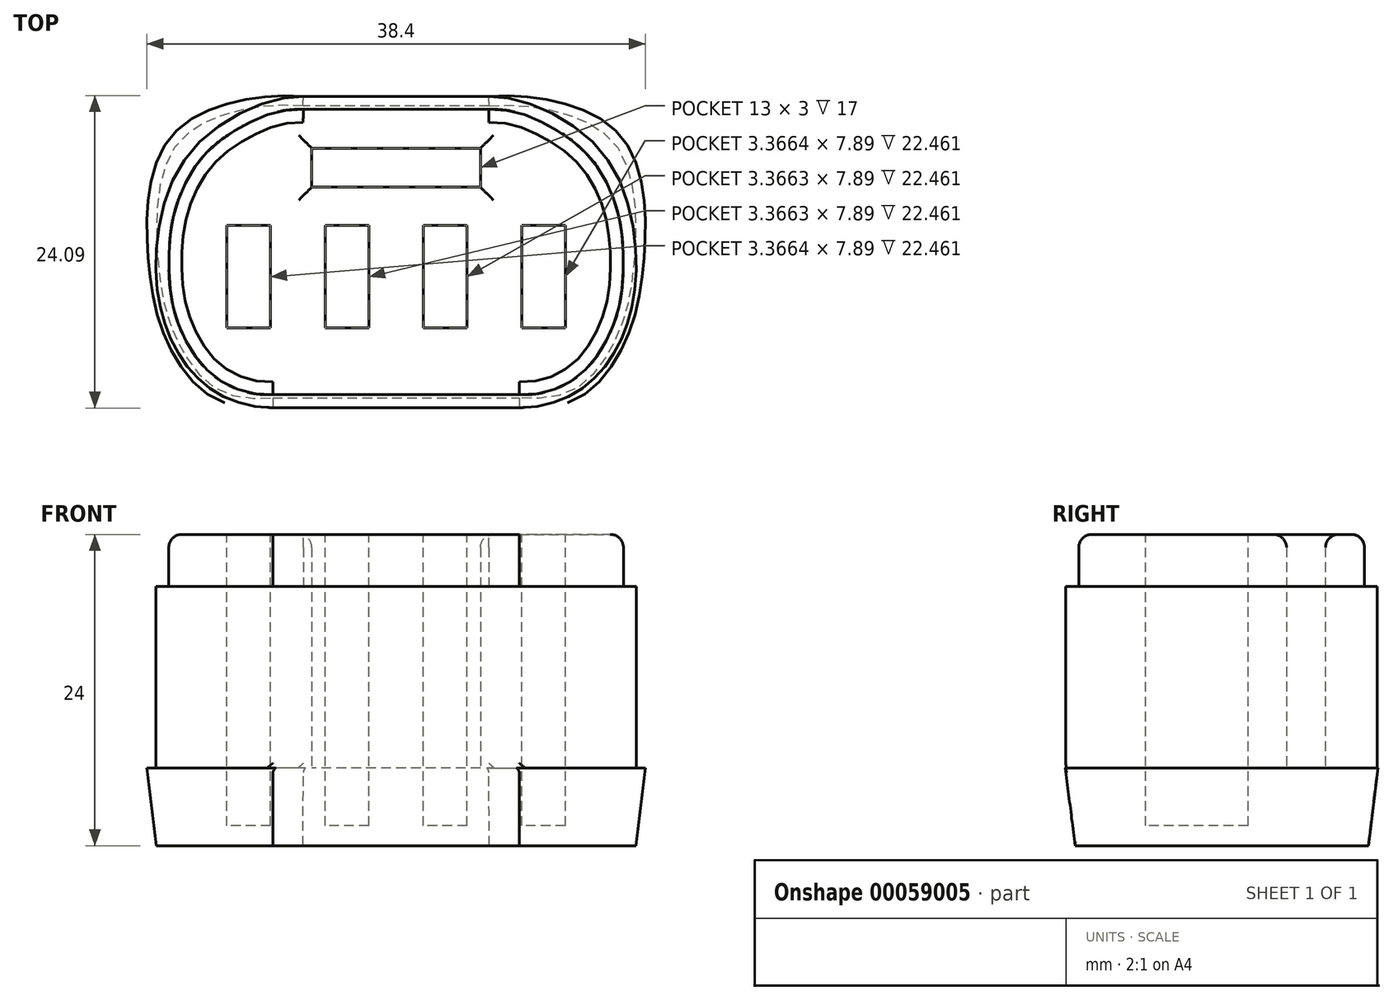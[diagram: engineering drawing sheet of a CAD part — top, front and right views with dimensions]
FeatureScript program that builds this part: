
annotation { "Feature Type Name" : "Feature", "Feature Type Description" : "" }
export const myFeature = defineFeature(function(context is Context, id is Id, definition is map)
    precondition{}
    {
        {
            var Q0;
            Q0=qCreatedBy(makeId("Top.planeOp"),FACE);
            var sketch = newSketch(context, id + "F0", { "sketchPlane" : qUnion([Q0])});
            skLineSegment(sketch, "E0", {"start": v(-18.5, 34.36) * mm, "end": v(18.5, 34.36) * mm, "construction": true});
            skLineSegment(sketch, "E1", {"start": v(0, 34.36) * mm, "end": v(0, 0) * mm, "construction": true});
            skLineSegment(sketch, "E2", {"start": v(0, 47.7) * mm, "end": v(0, 23.7) * mm, "construction": true});
            skLineSegment(sketch, "E3", {"start": v(0, 47.7) * mm, "end": v(7.15, 47.7) * mm});
            skLineSegment(sketch, "E4", {"start": v(0, 47.7) * mm, "end": v(-7.15, 47.7) * mm});
            skLineSegment(sketch, "E5", {"start": v(0, 23.7) * mm, "end": v(9.49, 23.7) * mm});
            skLineSegment(sketch, "E6", {"start": v(0, 23.7) * mm, "end": v(-9.49, 23.7) * mm});
            skFitSpline(sketch, "E7", {"points": [v(7.15, 47.7) * mm, v(15.73, 43.56) * mm, v(18.5, 34.36) * mm, v(17.25, 28.75) * mm, v(14.33, 25.17) * mm, v(9.49, 23.7) * mm], "startDerivative": vector(32.68, 0) * mm, "endDerivative": vector(-32.43, 0) * mm});
            skFitSpline(sketch, "E8.MirrorCS", {"points": [v(-7.15, 47.7) * mm, v(-15.73, 43.56) * mm, v(-18.5, 34.36) * mm, v(-17.25, 28.75) * mm, v(-14.33, 25.17) * mm, v(-9.49, 23.7) * mm], "startDerivative": vector(-32.68, 0) * mm, "endDerivative": vector(32.43, 0) * mm});
            skLineSegment(sketch, "E9.0", {"start": v(0, 46.7) * mm, "end": v(-7.15, 46.7) * mm});
            skFitSpline(sketch, "E10.0", {"points": [v(-7.15, 46.7) * mm, v(-7.73, 46.7) * mm, v(-9.1, 46.5) * mm, v(-11.02, 45.8) * mm, v(-12.5, 45) * mm, v(-13.55, 44.28) * mm, v(-14.5, 43.46) * mm, v(-15.28, 42.56) * mm, v(-15.93, 41.55) * mm, v(-16.64, 40.1) * mm, v(-17.22, 38.14) * mm, v(-17.47, 36.14) * mm, v(-17.51, 34.63) * mm, v(-17.48, 33.57) * mm, v(-17.38, 32.6) * mm, v(-17.22, 31.7) * mm, v(-17, 30.85) * mm, v(-16.74, 30.05) * mm, v(-16.41, 29.3) * mm, v(-15.9, 28.33) * mm, v(-15.16, 27.23) * mm, v(-14.06, 26.14) * mm, v(-12.76, 25.33) * mm, v(-11.24, 24.82) * mm, v(-10.1, 24.7) * mm, v(-9.49, 24.7) * mm]});
            skLineSegment(sketch, "E10.1", {"start": v(0, 46.7) * mm, "end": v(7.15, 46.7) * mm});
            skFitSpline(sketch, "E10.2", {"points": [v(7.15, 46.7) * mm, v(7.73, 46.7) * mm, v(9.1, 46.5) * mm, v(11.02, 45.8) * mm, v(12.5, 45) * mm, v(13.55, 44.28) * mm, v(14.5, 43.46) * mm, v(15.28, 42.56) * mm, v(15.93, 41.55) * mm, v(16.64, 40.1) * mm, v(17.22, 38.14) * mm, v(17.47, 36.14) * mm, v(17.51, 34.63) * mm, v(17.48, 33.57) * mm, v(17.38, 32.6) * mm, v(17.22, 31.7) * mm, v(17, 30.85) * mm, v(16.74, 30.05) * mm, v(16.41, 29.3) * mm, v(15.9, 28.33) * mm, v(15.16, 27.23) * mm, v(14.06, 26.14) * mm, v(12.76, 25.33) * mm, v(11.24, 24.82) * mm, v(10.1, 24.7) * mm, v(9.49, 24.7) * mm]});
            skLineSegment(sketch, "E10.3", {"start": v(0, 24.7) * mm, "end": v(9.49, 24.7) * mm});
            skLineSegment(sketch, "E10.4", {"start": v(0, 24.7) * mm, "end": v(-9.49, 24.7) * mm});
            skLineSegment(sketch, "E11.rect.bottom", {"start": v(6.5, 43.7) * mm, "end": v(-6.5, 43.7) * mm});
            skLineSegment(sketch, "E11.rect.top", {"start": v(6.5, 40.7) * mm, "end": v(-6.5, 40.7) * mm});
            skLineSegment(sketch, "E11.rect.left", {"start": v(6.5, 43.7) * mm, "end": v(6.5, 40.7) * mm});
            skLineSegment(sketch, "E11.rect.right", {"start": v(-6.5, 43.7) * mm, "end": v(-6.5, 40.7) * mm});
            skPoint(sketch, "E11.rect.middle", {"position": v(0, 42.2) * mm});
            skSolve(sketch);
        }
        {
            var Q0;
            Q0=makeQuery(id+"F0.imprint","IMPRINT",FACE,{"disambiguationData":[TD([[makeQuery(id+"F0.imprint","IMPRINT",EDGE,{"derivedFrom":sQuery(id+"F0.wireOp",EDGE,"E9.0")}),1.0]])]});
            extrude(context, id + "F1", {"entities" : qUnion([Q0]), "depth" : 8 * mm, "symmetric" : true});
        }
        {
            var Q0;
            Q0=makeQuery(id+"F0.imprint","IMPRINT",FACE,{"disambiguationData":[TD([[makeQuery(id+"F0.imprint","IMPRINT",EDGE,{"derivedFrom":sQuery(id+"F0.wireOp",EDGE,"E3")}),-1.0]])]});
            var Q1;
            Q1=makeQuery(id+"F0.imprint","IMPRINT",FACE,{"disambiguationData":[TD([[makeQuery(id+"F0.imprint","IMPRINT",EDGE,{"derivedFrom":sQuery(id+"F0.wireOp",EDGE,"E9.0")}),1.0]])]});
            extrude(context, id + "F2", {"entities" : qUnion([Q0, Q1]), "operationType" : NewBodyOperationType.ADD, "oppositeDirection" : true, "depth" : 14 * mm});
        }
        {
            var Q0;
            Q0=makeQuery(id+"F2.opExtrude","CAP_FACE",FACE,{"disambiguationData":[OSD([sQuery(id+"F0.wireOp",EDGE,"E3"),sQuery(id+"F0.wireOp",EDGE,"E4"),sQuery(id+"F0.wireOp",EDGE,"E5"),sQuery(id+"F0.wireOp",EDGE,"E6"),sQuery(id+"F0.wireOp",EDGE,"E7"),sQuery(id+"F0.wireOp",EDGE,"E8.MirrorCS"),sQuery(id+"F0.wireOp",EDGE,"E11.rect.bottom"),sQuery(id+"F0.wireOp",EDGE,"E11.rect.top"),sQuery(id+"F0.wireOp",EDGE,"E11.rect.left"),sQuery(id+"F0.wireOp",EDGE,"E11.rect.right")])],"isStart":false});
            var sketch = newSketch(context, id + "F3", { "sketchPlane" : qUnion([Q0])});
            skFitSpline(sketch, "E12.0", {"points": [v(-7.15, -47.7) * mm, v(-9.74, -47.7) * mm, v(-17.33, -44.62) * mm, v(-19.03, -34.4) * mm, v(-17.63, -28.74) * mm, v(-14.58, -24.74) * mm, v(-11.36, -23.7) * mm, v(-9.49, -23.7) * mm]});
            skLineSegment(sketch, "E12.1", {"start": v(0, -47.7) * mm, "end": v(-7.15, -47.7) * mm});
            skLineSegment(sketch, "E12.2", {"start": v(0, -47.7) * mm, "end": v(7.15, -47.7) * mm});
            skFitSpline(sketch, "E12.3", {"points": [v(7.15, -47.7) * mm, v(9.74, -47.7) * mm, v(17.33, -44.62) * mm, v(19.03, -34.4) * mm, v(17.63, -28.74) * mm, v(14.58, -24.74) * mm, v(11.36, -23.7) * mm, v(9.49, -23.7) * mm]});
            skLineSegment(sketch, "E12.4", {"start": v(0, -23.7) * mm, "end": v(9.49, -23.7) * mm});
            skLineSegment(sketch, "E12.5", {"start": v(0, -23.7) * mm, "end": v(-9.49, -23.7) * mm});
            skSolve(sketch);
        }
        {
            var Q0;
            Q0 = qSketchRegion(id + "F3", true);
            extrude(context, id + "F4", {"entities" : qUnion([Q0]), "operationType" : NewBodyOperationType.ADD, "depth" : 6 * mm, "hasDraft" : true, "draftAngle" : 7 * degree, "draftPullDirection" : true});
        }
        {
            var Q0;
            Q0=makeQuery(id+"F4.boolean.opBoolean","MERGE",EDGE,{"derivedFrom":[makeQuery(id+"F2.opExtrude","CAP_EDGE",EDGE,{"disambiguationData":[OSD([sQuery(id+"F0.wireOp",EDGE,"E7")])],"isStart":false}),makeQuery(id+"F4.opExtrude","CAP_EDGE",EDGE,{"disambiguationData":[OSD([sQuery(id+"F3.wireOp",EDGE,"E12.3")])],"isStart":true})]});
            var Q1;
            Q1=makeQuery(id+"F4.boolean.opBoolean","MERGE",EDGE,{"derivedFrom":[makeQuery(id+"F2.opExtrude","CAP_EDGE",EDGE,{"disambiguationData":[OSD([sQuery(id+"F0.wireOp",EDGE,"E3"),sQuery(id+"F0.wireOp",EDGE,"E4")])],"isStart":false}),makeQuery(id+"F4.opExtrude","CAP_EDGE",EDGE,{"disambiguationData":[OSD([sQuery(id+"F3.wireOp",EDGE,"E12.1"),sQuery(id+"F3.wireOp",EDGE,"E12.2")])],"isStart":true})]});
            var Q2;
            Q2=makeQuery(id+"F4.boolean.opBoolean","MERGE",EDGE,{"derivedFrom":[makeQuery(id+"F2.opExtrude","CAP_EDGE",EDGE,{"disambiguationData":[OSD([sQuery(id+"F0.wireOp",EDGE,"E8.MirrorCS")])],"isStart":false}),makeQuery(id+"F4.opExtrude","CAP_EDGE",EDGE,{"disambiguationData":[OSD([sQuery(id+"F3.wireOp",EDGE,"E12.0")])],"isStart":true})]});
            var Q3;
            Q3=makeQuery(id+"F4.boolean.opBoolean","MERGE",EDGE,{"derivedFrom":[makeQuery(id+"F2.opExtrude","CAP_EDGE",EDGE,{"disambiguationData":[OSD([sQuery(id+"F0.wireOp",EDGE,"E5"),sQuery(id+"F0.wireOp",EDGE,"E6")])],"isStart":false}),makeQuery(id+"F4.opExtrude","CAP_EDGE",EDGE,{"disambiguationData":[OSD([sQuery(id+"F3.wireOp",EDGE,"E12.4"),sQuery(id+"F3.wireOp",EDGE,"E12.5")])],"isStart":true})]});
            fillet(context, id + "F5", {"entities" : qUnion([Q0, Q1, Q2, Q3]), "radius" : 6 * mm, "tangentPropagation" : true, "allowEdgeOverflow" : false});
        }
        {
            var Q0;
            Q0=makeQuery(id+"F1.opExtrude","CAP_EDGE",EDGE,{"disambiguationData":[OSD([sQuery(id+"F0.wireOp",EDGE,"E9.0"),sQuery(id+"F0.wireOp",EDGE,"E10.1")])],"isStart":false});
            var Q1;
            Q1=makeQuery(id+"F1.opExtrude","CAP_EDGE",EDGE,{"disambiguationData":[OSD([sQuery(id+"F0.wireOp",EDGE,"E11.rect.right")])],"isStart":false});
            var Q2;
            Q2=makeQuery(id+"F1.opExtrude","CAP_EDGE",EDGE,{"disambiguationData":[OSD([sQuery(id+"F0.wireOp",EDGE,"E11.rect.top")])],"isStart":false});
            var Q3;
            Q3=makeQuery(id+"F1.opExtrude","CAP_EDGE",EDGE,{"disambiguationData":[OSD([sQuery(id+"F0.wireOp",EDGE,"E11.rect.bottom")])],"isStart":false});
            var Q4;
            Q4=makeQuery(id+"F1.opExtrude","CAP_EDGE",EDGE,{"disambiguationData":[OSD([sQuery(id+"F0.wireOp",EDGE,"E11.rect.left")])],"isStart":false});
            fillet(context, id + "F6", {"entities" : qUnion([Q0, Q1, Q2, Q3, Q4]), "radius" : 1 * mm, "tangentPropagation" : true, "allowEdgeOverflow" : false});
        }
        {
            var Q0;
            Q0=makeQuery(id+"F1.opExtrude","CAP_FACE",FACE,{"disambiguationData":[OSD([sQuery(id+"F0.wireOp",EDGE,"E9.0"),sQuery(id+"F0.wireOp",EDGE,"E10.0"),sQuery(id+"F0.wireOp",EDGE,"E10.1"),sQuery(id+"F0.wireOp",EDGE,"E10.2"),sQuery(id+"F0.wireOp",EDGE,"E10.3"),sQuery(id+"F0.wireOp",EDGE,"E10.4"),sQuery(id+"F0.wireOp",EDGE,"E11.rect.bottom"),sQuery(id+"F0.wireOp",EDGE,"E11.rect.top"),sQuery(id+"F0.wireOp",EDGE,"E11.rect.left"),sQuery(id+"F0.wireOp",EDGE,"E11.rect.right")])],"isStart":false});
            var sketch = newSketch(context, id + "F7", { "sketchPlane" : qUnion([Q0])});
            skLineSegment(sketch, "E13", {"start": v(-13.04, 33.8) * mm, "end": v(13.04, 33.8) * mm, "construction": true});
            skLineSegment(sketch, "E14.rect.bottom", {"start": v(-9.68, 37.74) * mm, "end": v(-13.04, 37.74) * mm});
            skLineSegment(sketch, "E14.rect.top", {"start": v(-9.68, 29.85) * mm, "end": v(-13.04, 29.85) * mm});
            skLineSegment(sketch, "E14.rect.left", {"start": v(-9.68, 37.74) * mm, "end": v(-9.68, 29.85) * mm});
            skLineSegment(sketch, "E14.rect.right", {"start": v(-13.04, 37.74) * mm, "end": v(-13.04, 29.85) * mm});
            skPoint(sketch, "E14.rect.middle", {"position": v(-11.36, 33.8) * mm});
            skLineSegment(sketch, "E15.rect.bottom", {"start": v(-2.1, 37.74) * mm, "end": v(-5.47, 37.74) * mm});
            skLineSegment(sketch, "E15.rect.top", {"start": v(-2.1, 29.85) * mm, "end": v(-5.47, 29.85) * mm});
            skLineSegment(sketch, "E15.rect.left", {"start": v(-2.1, 37.74) * mm, "end": v(-2.1, 29.85) * mm});
            skLineSegment(sketch, "E15.rect.right", {"start": v(-5.47, 37.74) * mm, "end": v(-5.47, 29.85) * mm});
            skPoint(sketch, "E15.rect.middle", {"position": v(-3.79, 33.8) * mm});
            skLineSegment(sketch, "E16.rect.bottom", {"start": v(5.47, 37.74) * mm, "end": v(2.1, 37.74) * mm});
            skLineSegment(sketch, "E16.rect.top", {"start": v(5.47, 29.85) * mm, "end": v(2.1, 29.85) * mm});
            skLineSegment(sketch, "E16.rect.left", {"start": v(5.47, 37.74) * mm, "end": v(5.47, 29.85) * mm});
            skLineSegment(sketch, "E16.rect.right", {"start": v(2.1, 37.74) * mm, "end": v(2.1, 29.85) * mm});
            skPoint(sketch, "E16.rect.middle", {"position": v(3.79, 33.8) * mm});
            skLineSegment(sketch, "E17.rect.bottom", {"start": v(13.04, 37.74) * mm, "end": v(9.68, 37.74) * mm});
            skLineSegment(sketch, "E17.rect.top", {"start": v(13.04, 29.85) * mm, "end": v(9.68, 29.85) * mm});
            skLineSegment(sketch, "E17.rect.left", {"start": v(13.04, 37.74) * mm, "end": v(13.04, 29.85) * mm});
            skLineSegment(sketch, "E17.rect.right", {"start": v(9.68, 37.74) * mm, "end": v(9.68, 29.85) * mm});
            skPoint(sketch, "E17.rect.middle", {"position": v(11.36, 33.8) * mm});
            skLineSegment(sketch, "E18", {"start": v(-9.68, 37.74) * mm, "end": v(-5.47, 37.74) * mm, "construction": true});
            skLineSegment(sketch, "E19", {"start": v(-2.1, 37.74) * mm, "end": v(2.1, 37.74) * mm, "construction": true});
            skLineSegment(sketch, "E20", {"start": v(5.47, 37.74) * mm, "end": v(9.68, 37.74) * mm, "construction": true});
            skLineSegment(sketch, "E21", {"start": v(0, 33.8) * mm, "end": v(0, 39.7) * mm});
            skSolve(sketch);
        }
        {
            var Q0;
            Q0=makeQuery(id+"F7.imprint","IMPRINT",FACE,{"disambiguationData":[TD([[makeQuery(id+"F7.imprint","IMPRINT",EDGE,{"derivedFrom":sQuery(id+"F7.wireOp",EDGE,"E14.rect.bottom")}),1.0]])]});
            var Q1;
            Q1=makeQuery(id+"F7.imprint","IMPRINT",FACE,{"disambiguationData":[TD([[makeQuery(id+"F7.imprint","IMPRINT",EDGE,{"derivedFrom":sQuery(id+"F7.wireOp",EDGE,"E15.rect.bottom")}),1.0]])]});
            var Q2;
            Q2=makeQuery(id+"F7.imprint","IMPRINT",FACE,{"disambiguationData":[TD([[makeQuery(id+"F7.imprint","IMPRINT",EDGE,{"derivedFrom":sQuery(id+"F7.wireOp",EDGE,"E16.rect.bottom")}),1.0]])]});
            var Q3;
            Q3=makeQuery(id+"F7.imprint","IMPRINT",FACE,{"disambiguationData":[TD([[makeQuery(id+"F7.imprint","IMPRINT",EDGE,{"derivedFrom":sQuery(id+"F7.wireOp",EDGE,"E17.rect.bottom")}),1.0]])]});
            extrude(context, id + "F8", {"entities" : qUnion([Q0, Q1, Q2, Q3]), "operationType" : NewBodyOperationType.REMOVE, "oppositeDirection" : true, "depth" : 22.46 * mm});
        }
    });
